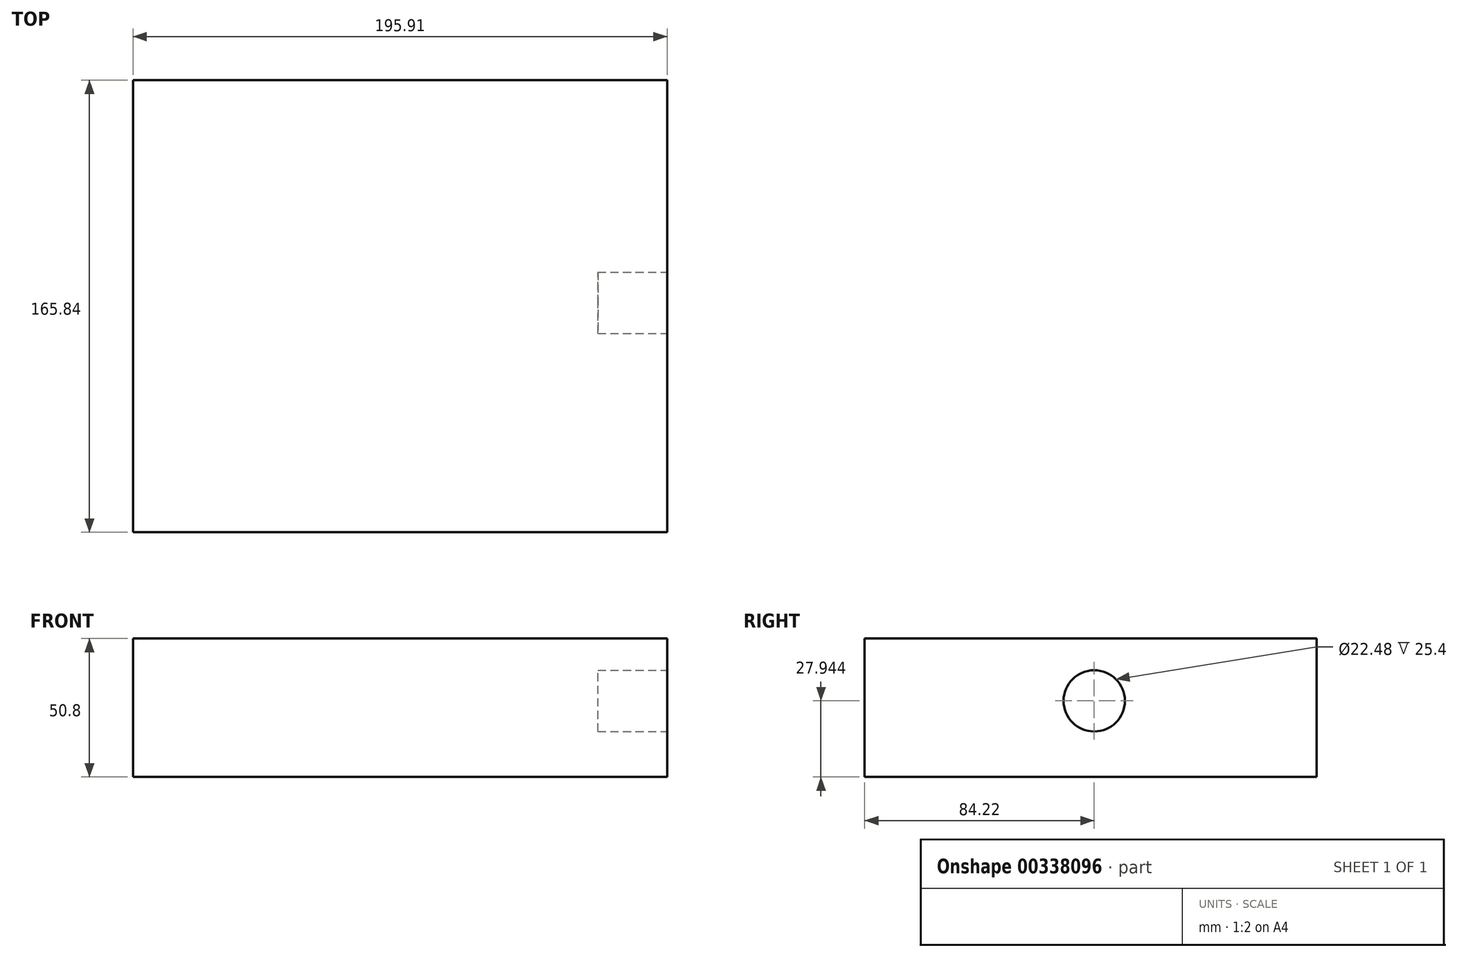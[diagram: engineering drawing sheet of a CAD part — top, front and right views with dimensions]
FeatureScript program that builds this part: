
annotation { "Feature Type Name" : "Feature", "Feature Type Description" : "" }
export const myFeature = defineFeature(function(context is Context, id is Id, definition is map)
    precondition{}
    {
        {
            var Q0;
            Q0=qCreatedBy(makeId("Top.planeOp"),FACE);
            var sketch = newSketch(context, id + "F0", { "sketchPlane" : qUnion([Q0])});
            skLineSegment(sketch, "E0.bottom", {"start": v(-89.4, 76.28) * mm, "end": v(106.5, 76.28) * mm});
            skLineSegment(sketch, "E0.top", {"start": v(-89.4, -89.56) * mm, "end": v(106.5, -89.56) * mm});
            skLineSegment(sketch, "E0.left", {"start": v(-89.4, 76.28) * mm, "end": v(-89.4, -89.56) * mm});
            skLineSegment(sketch, "E0.right", {"start": v(106.5, 76.28) * mm, "end": v(106.5, -89.56) * mm});
            skSolve(sketch);
        }
        {
            var Q0;
            Q0 = qSketchRegion(id + "F0", true);
            extrude(context, id + "F1", {"entities" : qUnion([Q0]), "depth" : 50.8 * mm});
        }
        {
            var Q0;
            Q0=makeQuery(id+"F1.opExtrude","SWEPT_FACE",FACE,{"disambiguationData":[OSD([sQuery(id+"F0.wireOp",EDGE,"E0.right")])]});
            var sketch = newSketch(context, id + "F2", { "sketchPlane" : qUnion([Q0])});
            skCircle(sketch, "E1", {"center": v(-5.34, 27.94) * mm, "radius": 11.24 * mm});
            skSolve(sketch);
        }
        {
            var Q0;
            Q0=makeQuery(id+"F2.imprint","IMPRINT",FACE,{"disambiguationData":[TD([[makeQuery(id+"F2.imprint","IMPRINT",EDGE,{"derivedFrom":sQuery(id+"F2.wireOp",EDGE,"E1")}),1.0]])]});
            extrude(context, id + "F3", {"entities" : qUnion([Q0]), "operationType" : NewBodyOperationType.REMOVE, "oppositeDirection" : true, "depth" : 25.4 * mm});
        }
    });
